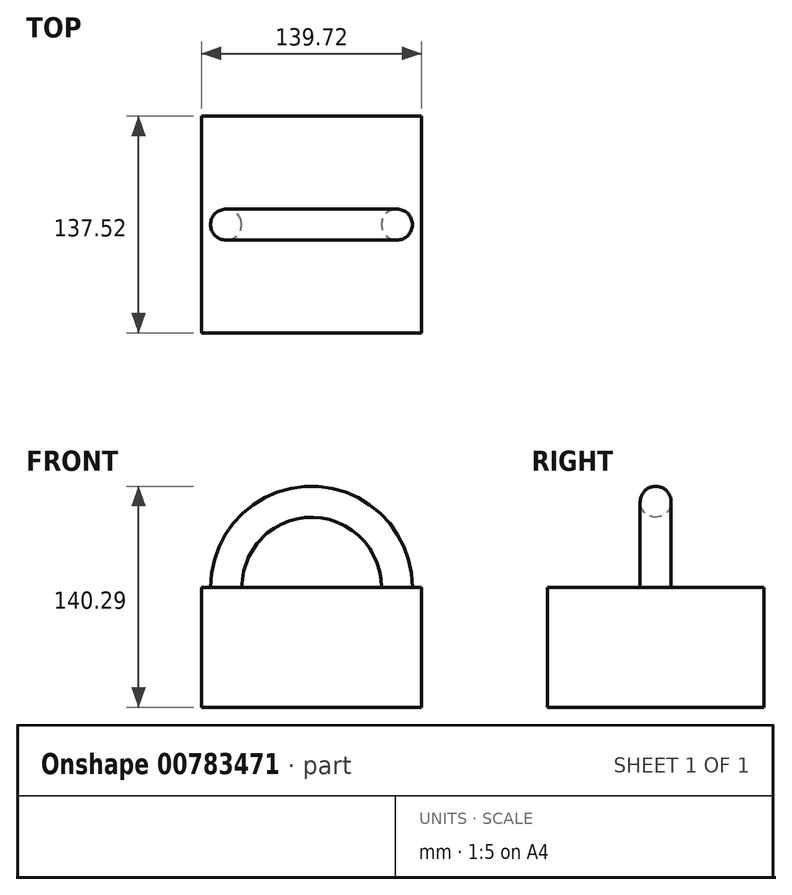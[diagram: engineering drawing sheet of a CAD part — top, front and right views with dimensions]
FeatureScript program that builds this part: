
annotation { "Feature Type Name" : "Feature", "Feature Type Description" : "" }
export const myFeature = defineFeature(function(context is Context, id is Id, definition is map)
    precondition{}
    {
        {
            var Q0;
            Q0=qCreatedBy(makeId("Top.planeOp"),FACE);
            var sketch = newSketch(context, id + "F0", { "sketchPlane" : qUnion([Q0])});
            skLineSegment(sketch, "E0.bottom", {"start": v(69.86, -68.76) * mm, "end": v(-69.86, -68.76) * mm});
            skLineSegment(sketch, "E0.top", {"start": v(69.86, 68.76) * mm, "end": v(-69.86, 68.76) * mm});
            skLineSegment(sketch, "E0.left", {"start": v(69.86, -68.76) * mm, "end": v(69.86, 68.76) * mm});
            skLineSegment(sketch, "E0.right", {"start": v(-69.86, -68.76) * mm, "end": v(-69.86, 68.76) * mm});
            skPoint(sketch, "E0.middle", {"position": v(0, 0) * mm});
            skLineSegment(sketch, "E1", {"start": v(0, 68.76) * mm, "end": v(0, -68.76) * mm});
            skSolve(sketch);
        }
        {
            var Q0;
            Q0=qCreatedBy(makeId("Top.planeOp"),FACE);
            var sketch = newSketch(context, id + "F1", { "sketchPlane" : qUnion([Q0])});
            skCircle(sketch, "E2", {"center": v(54.26, 0) * mm, "radius": 9.82 * mm});
            skSolve(sketch);
        }
        {
            var Q0;
            Q0 = qSketchRegion(id + "F1", true);
            var Q1;
            Q1=sQuery(id+"F0.wireOp",EDGE,"E1");
            revolve(context, id + "F2", {"surfaceOperationType" : NewSurfaceOperationType.NEW, "entities" : qUnion([Q0]), "axis" : qUnion([Q1]), "revolveType" : RevolveType.FULL});
        }
        {
            var Q0;
            {var subQ0=sQuery(id+"F0.wireOp",EDGE,"E0.right");Q0=makeQuery(id+"F0.imprint","IMPRINT",FACE,{"disambiguationData":[TD([[makeQuery(id+"F0.imprint","IMPRINT",EDGE,{"derivedFrom":subQ0}),-1.0]])]});}
            var Q1;
            {var subQ0=sQuery(id+"F0.wireOp",EDGE,"E0.left");Q1=makeQuery(id+"F0.imprint","IMPRINT",FACE,{"disambiguationData":[TD([[makeQuery(id+"F0.imprint","IMPRINT",EDGE,{"derivedFrom":subQ0}),1.0]])]});}
            extrude(context, id + "F3", {"entities" : qUnion([Q0, Q1]), "operationType" : NewBodyOperationType.ADD, "oppositeDirection" : true, "depth" : 76.2 * mm, "offsetDistance" : 25.4 * mm});
        }
    });
